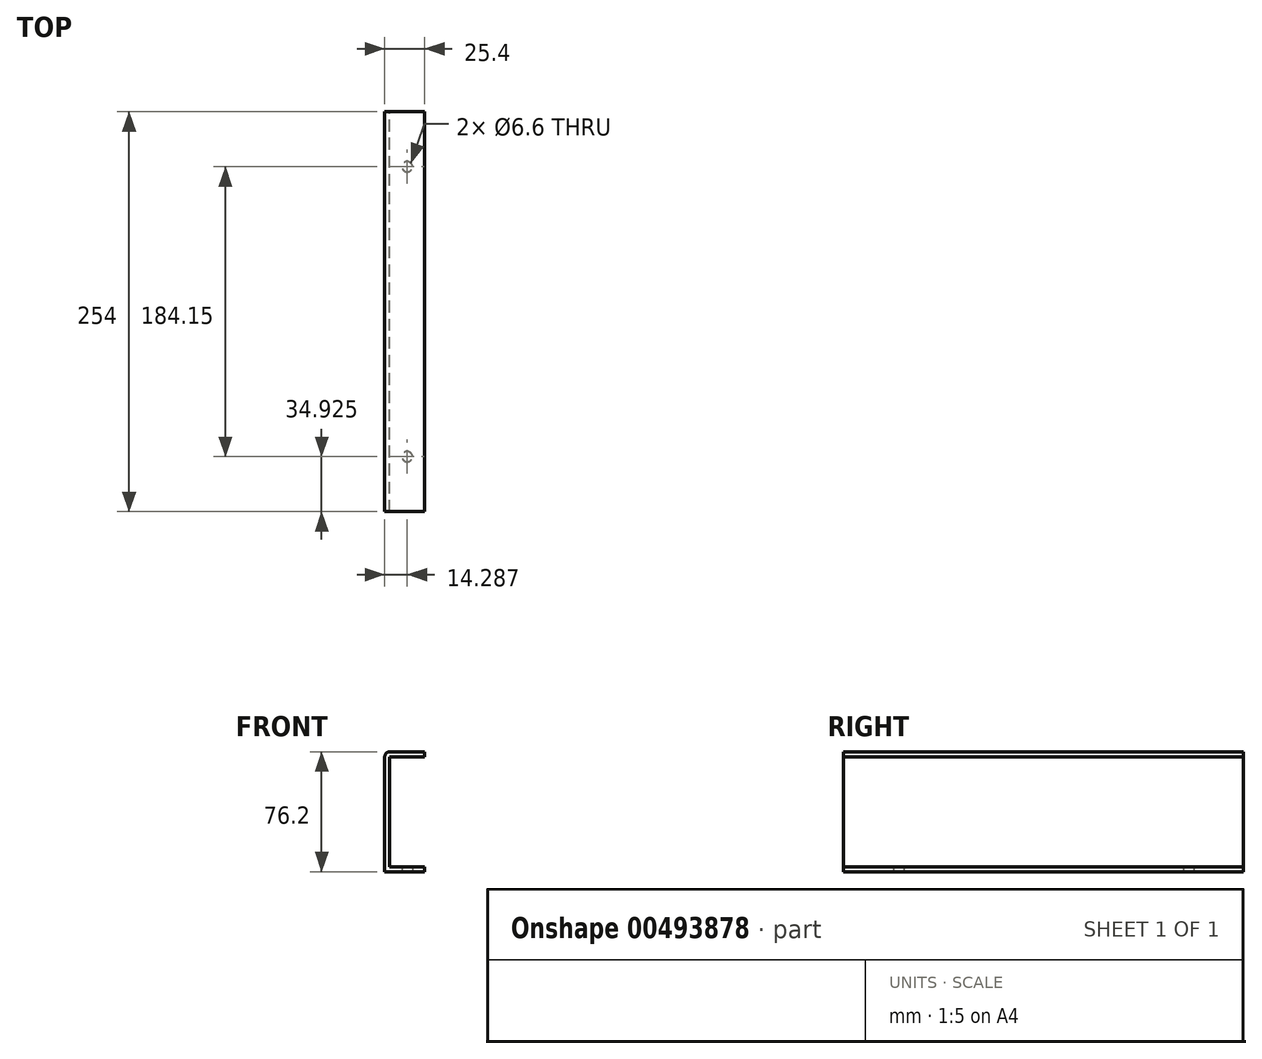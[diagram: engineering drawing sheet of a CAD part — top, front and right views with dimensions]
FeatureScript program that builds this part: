
annotation { "Feature Type Name" : "Feature", "Feature Type Description" : "" }
export const myFeature = defineFeature(function(context is Context, id is Id, definition is map)
    precondition{}
    {
        {
            var Q0;
            Q0=qCreatedBy(makeId("Front.planeOp"),FACE);
            var sketch = newSketch(context, id + "F0", { "sketchPlane" : qUnion([Q0])});
            skLineSegment(sketch, "E0", {"start": v(0, 38.1) * mm, "end": v(-25.4, 38.1) * mm});
            skLineSegment(sketch, "E1", {"start": v(-25.4, 38.1) * mm, "end": v(-25.4, -38.1) * mm});
            skLineSegment(sketch, "E2", {"start": v(-25.4, -38.1) * mm, "end": v(0, -38.1) * mm});
            skLineSegment(sketch, "E3", {"start": v(0, -38.1) * mm, "end": v(0, -34.93) * mm});
            skLineSegment(sketch, "E4", {"start": v(0, -34.93) * mm, "end": v(-22.22, -34.93) * mm});
            skLineSegment(sketch, "E5", {"start": v(-22.22, -34.93) * mm, "end": v(-22.22, 34.93) * mm});
            skLineSegment(sketch, "E6", {"start": v(-22.22, 34.93) * mm, "end": v(0, 34.93) * mm});
            skLineSegment(sketch, "E7", {"start": v(0, 34.93) * mm, "end": v(0, 38.1) * mm});
            skSolve(sketch);
        }
        {
            var Q0;
            Q0=makeQuery(id+"F0.imprint","IMPRINT",FACE,{"disambiguationData":[TD([[makeQuery(id+"F0.imprint","IMPRINT",EDGE,{"derivedFrom":sQuery(id+"F0.wireOp",EDGE,"E0")}),1.0]])]});
            extrude(context, id + "F1", {"entities" : qUnion([Q0]), "depth" : 254 * mm});
        }
        {
            var Q0;
            Q0=makeQuery(id+"F1.opExtrude","SWEPT_FACE",FACE,{"disambiguationData":[OSD([sQuery(id+"F0.wireOp",EDGE,"E2")])]});
            var sketch = newSketch(context, id + "F2", { "sketchPlane" : qUnion([Q0])});
            skLineSegment(sketch, "E8.0", {"start": v(-22.22, 254) * mm, "end": v(-22.22, 0) * mm});
            skLineSegment(sketch, "E9", {"start": v(-22.22, 127) * mm, "end": v(0, 127) * mm, "construction": true});
            skLineSegment(sketch, "E10", {"start": v(-11.11, 219.08) * mm, "end": v(-11.11, 34.92) * mm, "construction": true});
            skPoint(sketch, "E11", {"position": v(-11.11, 127) * mm});
            skSolve(sketch);
        }
        {
            var Q0;
            Q0=sQuery(id+"F2.wireOp",VERTEX,"E10.start");
            var Q1;
            Q1=sQuery(id+"F2.wireOp",VERTEX,"E10.end");
            var Q2;
            Q2=makeQuery(id+"F1.opExtrude","SWEPT_BODY",BODY,{"disambiguationData":[OSD([sQuery(id+"F0.wireOp",EDGE,"E0"),sQuery(id+"F0.wireOp",EDGE,"E1"),sQuery(id+"F0.wireOp",EDGE,"E2"),sQuery(id+"F0.wireOp",EDGE,"E3"),sQuery(id+"F0.wireOp",EDGE,"E4"),sQuery(id+"F0.wireOp",EDGE,"E5"),sQuery(id+"F0.wireOp",EDGE,"E6"),sQuery(id+"F0.wireOp",EDGE,"E7")])]});
            hole(context, id + "F3", {"style" : HoleStyle.SIMPLE, "endStyle" : HoleEndStyle.BLIND, "standardTappedOrClearance" : lookupTablePath({ "standard" : "ISO", "fit" : "Normal", "size" : "M6", "type" : "Clearance" }), "standardBlindInLast" : lookupTablePath({ "fit" : "Standard", "standard" : "ISO", "size" : "M6", "type" : "Clearance" }), "holeDiameter" : 6.6 * mm, "holeDepth" : 15 * mm, "isTappedThrough" : true, "tappedDepth" : 12.7 * mm, "tapClearance" : 3, "locations" : qUnion([Q0, Q1]), "scope" : qUnion([Q2])});
        }
        {
            var Q0;
            Q0=makeQuery(id+"F1.opExtrude","SWEPT_EDGE",EDGE,{"disambiguationData":[OSD([sQuery(id+"F0.wireOp",EDGE,"E0"),sQuery(id+"F0.wireOp",EDGE,"E1")])]});
            fillet(context, id + "F4", {"entities" : qUnion([Q0]), "radius" : 3.17 * mm, "tangentPropagation" : true, "allowEdgeOverflow" : false});
        }
    });
